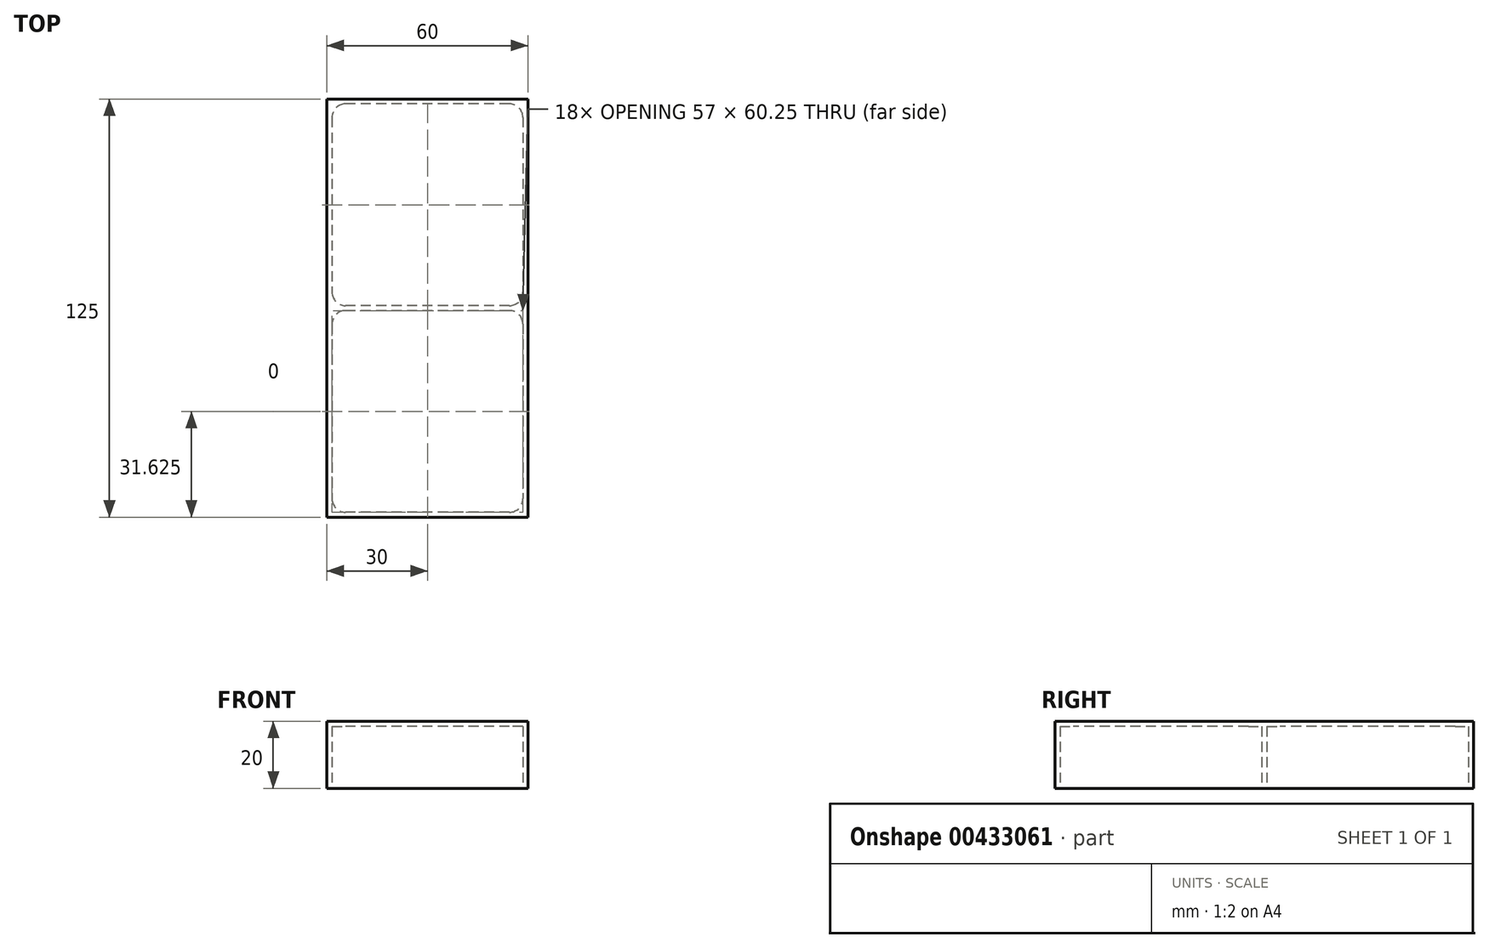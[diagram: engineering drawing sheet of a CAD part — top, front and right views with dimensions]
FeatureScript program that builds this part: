
annotation { "Feature Type Name" : "Feature", "Feature Type Description" : "" }
export const myFeature = defineFeature(function(context is Context, id is Id, definition is map)
    precondition{}
    {
        {
            var Q0;
            Q0=qCreatedBy(makeId("Top.planeOp"),FACE);
            var sketch = newSketch(context, id + "F0", { "sketchPlane" : qUnion([Q0])});
            skLineSegment(sketch, "E0.bottom", {"start": v(30, 62.5) * mm, "end": v(-30, 62.5) * mm});
            skLineSegment(sketch, "E0.top", {"start": v(30, -62.5) * mm, "end": v(-30, -62.5) * mm});
            skLineSegment(sketch, "E0.left", {"start": v(30, 62.5) * mm, "end": v(30, -62.5) * mm});
            skLineSegment(sketch, "E0.right", {"start": v(-30, 62.5) * mm, "end": v(-30, -62.5) * mm});
            skPoint(sketch, "E0.middle", {"position": v(0, 0) * mm});
            skSolve(sketch);
        }
        {
            var Q0;
            Q0 = qSketchRegion(id + "F0", true);
            extrude(context, id + "F1", {"entities" : qUnion([Q0]), "depth" : 20 * mm});
        }
        {
            var Q0;
            Q0=qCreatedBy(makeId("Top.planeOp"),FACE);
            var sketch = newSketch(context, id + "F2", { "sketchPlane" : qUnion([Q0])});
            skLineSegment(sketch, "E1.bottom", {"start": v(28.5, 61) * mm, "end": v(-28.5, 61) * mm});
            skLineSegment(sketch, "E1.top", {"start": v(28.5, 0.75) * mm, "end": v(-28.5, 0.75) * mm});
            skLineSegment(sketch, "E1.left", {"start": v(28.5, 61) * mm, "end": v(28.5, 0.75) * mm});
            skLineSegment(sketch, "E1.right", {"start": v(-28.5, 61) * mm, "end": v(-28.5, 0.75) * mm});
            skLineSegment(sketch, "E2.bottom", {"start": v(28.5, -0.75) * mm, "end": v(-28.5, -0.75) * mm});
            skLineSegment(sketch, "E2.top", {"start": v(28.5, -61) * mm, "end": v(-28.5, -61) * mm});
            skLineSegment(sketch, "E2.left", {"start": v(28.5, -0.75) * mm, "end": v(28.5, -61) * mm});
            skLineSegment(sketch, "E2.right", {"start": v(-28.5, -0.75) * mm, "end": v(-28.5, -61) * mm});
            skSolve(sketch);
        }
        {
            var Q0;
            Q0 = qSketchRegion(id + "F2", true);
            extrude(context, id + "F3", {"entities" : qUnion([Q0]), "operationType" : NewBodyOperationType.REMOVE, "depth" : 18.5 * mm});
        }
        {
            var Q0;
            Q0=makeQuery(id+"F3.boolean.opBoolean","COPY",EDGE,{"derivedFrom":makeQuery(id+"F3.opExtrude","SWEPT_EDGE",EDGE,{"disambiguationData":[OSD([sQuery(id+"F2.wireOp",EDGE,"E2.top"),sQuery(id+"F2.wireOp",EDGE,"E2.left")])]})});
            var Q1;
            Q1=makeQuery(id+"F3.boolean.opBoolean","COPY",EDGE,{"derivedFrom":makeQuery(id+"F3.opExtrude","SWEPT_EDGE",EDGE,{"disambiguationData":[OSD([sQuery(id+"F2.wireOp",EDGE,"E1.top"),sQuery(id+"F2.wireOp",EDGE,"E1.left")])]})});
            var Q2;
            Q2=makeQuery(id+"F3.boolean.opBoolean","COPY",EDGE,{"derivedFrom":makeQuery(id+"F3.opExtrude","SWEPT_EDGE",EDGE,{"disambiguationData":[OSD([sQuery(id+"F2.wireOp",EDGE,"E2.top"),sQuery(id+"F2.wireOp",EDGE,"E2.right")])]})});
            var Q3;
            Q3=makeQuery(id+"F3.boolean.opBoolean","COPY",EDGE,{"derivedFrom":makeQuery(id+"F3.opExtrude","SWEPT_EDGE",EDGE,{"disambiguationData":[OSD([sQuery(id+"F2.wireOp",EDGE,"E1.top"),sQuery(id+"F2.wireOp",EDGE,"E1.right")])]})});
            var Q4;
            Q4=makeQuery(id+"F3.boolean.opBoolean","COPY",EDGE,{"derivedFrom":makeQuery(id+"F3.opExtrude","SWEPT_EDGE",EDGE,{"disambiguationData":[OSD([sQuery(id+"F2.wireOp",EDGE,"E2.bottom"),sQuery(id+"F2.wireOp",EDGE,"E2.right")])]})});
            var Q5;
            Q5=makeQuery(id+"F3.boolean.opBoolean","COPY",EDGE,{"derivedFrom":makeQuery(id+"F3.opExtrude","SWEPT_EDGE",EDGE,{"disambiguationData":[OSD([sQuery(id+"F2.wireOp",EDGE,"E1.bottom"),sQuery(id+"F2.wireOp",EDGE,"E1.right")])]})});
            var Q6;
            Q6=makeQuery(id+"F3.boolean.opBoolean","COPY",EDGE,{"derivedFrom":makeQuery(id+"F3.opExtrude","SWEPT_EDGE",EDGE,{"disambiguationData":[OSD([sQuery(id+"F2.wireOp",EDGE,"E1.bottom"),sQuery(id+"F2.wireOp",EDGE,"E1.left")])]})});
            var Q7;
            Q7=makeQuery(id+"F3.boolean.opBoolean","COPY",EDGE,{"derivedFrom":makeQuery(id+"F3.opExtrude","SWEPT_EDGE",EDGE,{"disambiguationData":[OSD([sQuery(id+"F2.wireOp",EDGE,"E2.bottom"),sQuery(id+"F2.wireOp",EDGE,"E2.left")])]})});
            fillet(context, id + "F4", {"entities" : qUnion([Q0, Q1, Q2, Q3, Q4, Q5, Q6, Q7]), "radius" : 4 * mm, "tangentPropagation" : true, "allowEdgeOverflow" : false});
        }
    });
